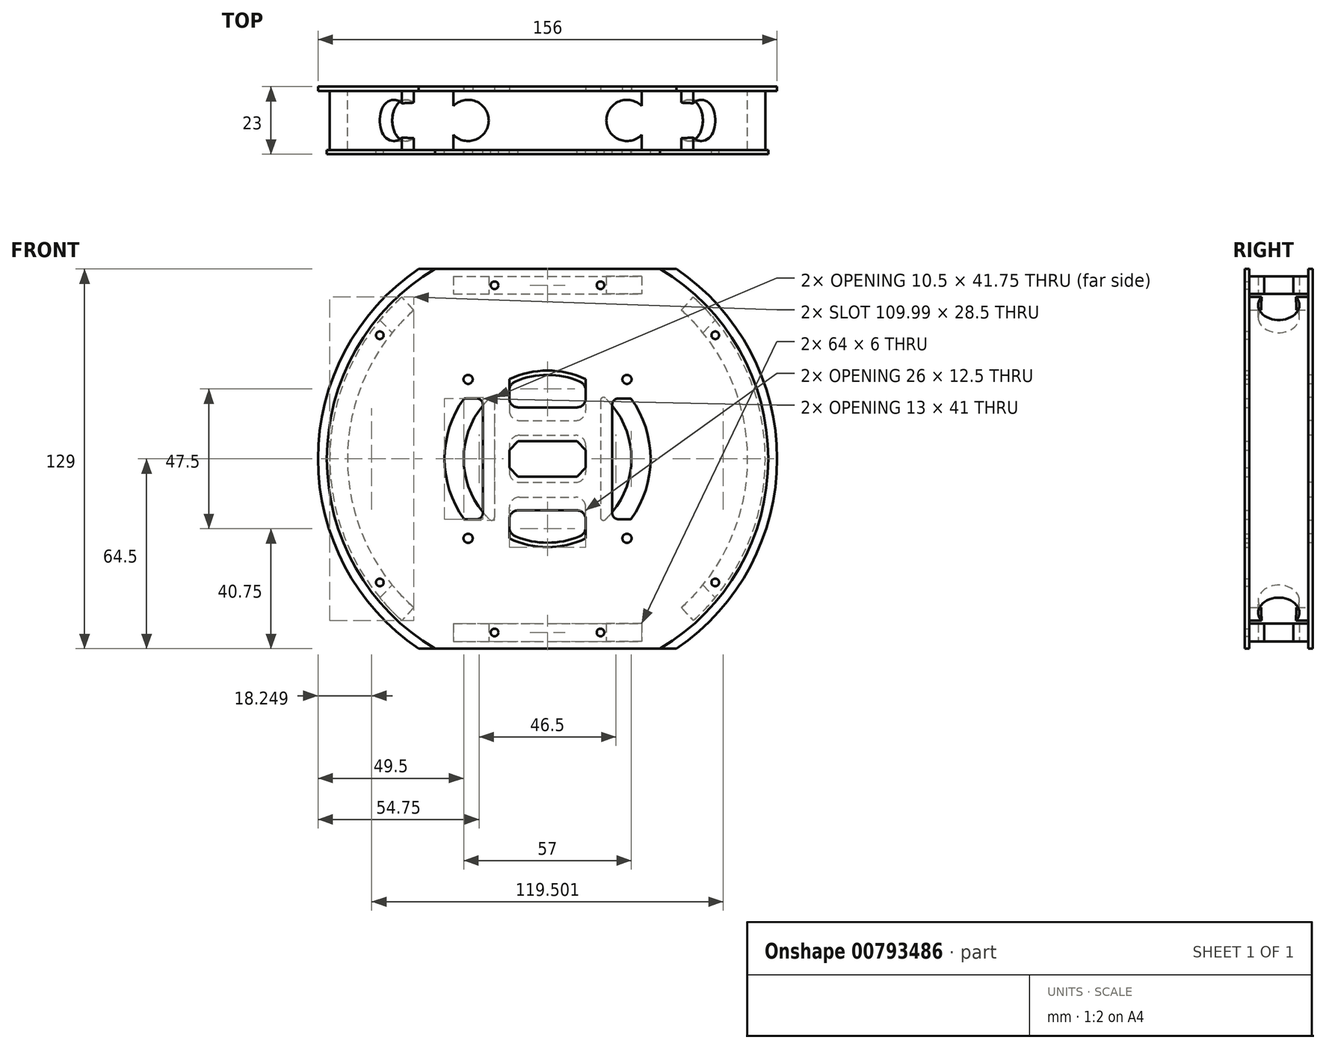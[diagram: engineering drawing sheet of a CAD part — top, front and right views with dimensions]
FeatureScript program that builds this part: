
annotation { "Feature Type Name" : "Feature", "Feature Type Description" : "" }
export const myFeature = defineFeature(function(context is Context, id is Id, definition is map)
    precondition{}
    {
        {
            var Q0;
            Q0=qCreatedBy(makeId("Front.planeOp"),FACE);
            var sketch = newSketch(context, id + "F0", { "sketchPlane" : qUnion([Q0])});
            skLineSegment(sketch, "E0", {"start": v(-78, 0) * mm, "end": v(78, 0) * mm, "construction": true});
            skArc(sketch, "E1", {"start": v(-43.86, 64.5) * mm, "mid": v(-78, 0) * mm, "end": v(-43.86, -64.5) * mm});
            skLineSegment(sketch, "E2", {"start": v(0, 78) * mm, "end": v(0, -78) * mm, "construction": true});
            skLineSegment(sketch, "E3", {"start": v(-43.86, 64.5) * mm, "end": v(43.86, 64.5) * mm});
            skLineSegment(sketch, "E4", {"start": v(-43.86, -64.5) * mm, "end": v(43.86, -64.5) * mm});
            skArc(sketch, "E5.trimOffspring", {"start": v(43.86, -64.5) * mm, "mid": v(78, 0) * mm, "end": v(43.86, 64.5) * mm});
            skLineSegment(sketch, "E6.bottom", {"start": v(-9.5, 8) * mm, "end": v(9.5, 8) * mm});
            skLineSegment(sketch, "E6.top", {"start": v(-9.5, -8) * mm, "end": v(9.5, -8) * mm});
            skLineSegment(sketch, "E6.left", {"start": v(-13, 4.5) * mm, "end": v(-13, -4.5) * mm});
            skLineSegment(sketch, "E6.right", {"start": v(13, 4.5) * mm, "end": v(13, -4.5) * mm});
            skPoint(sketch, "E7.visualSharp", {"position": v(-13, 8) * mm});
            skArc(sketch, "E7.filletArc", {"start": v(-9.5, 8) * mm, "mid": v(-11.97, 6.97) * mm, "end": v(-13, 4.5) * mm});
            skArc(sketch, "E8.MirrorCS", {"start": v(9.5, 8) * mm, "mid": v(11.97, 6.97) * mm, "end": v(13, 4.5) * mm});
            skArc(sketch, "E9.MirrorCS", {"start": v(9.5, -8) * mm, "mid": v(11.97, -6.97) * mm, "end": v(13, -4.5) * mm});
            skArc(sketch, "E10.MirrorCS", {"start": v(-9.5, -8) * mm, "mid": v(-11.97, -6.97) * mm, "end": v(-13, -4.5) * mm});
            skLineSegment(sketch, "E11.top", {"start": v(-9.5, 13) * mm, "end": v(9.5, 13) * mm});
            skLineSegment(sketch, "E11.left", {"start": v(-13, 23.12) * mm, "end": v(-13, 16.5) * mm});
            skLineSegment(sketch, "E11.right", {"start": v(13, 23.12) * mm, "end": v(13, 16.5) * mm});
            skArc(sketch, "E12", {"start": v(-19.7, 20.6) * mm, "mid": v(-28.5, 0) * mm, "end": v(-19.7, -20.6) * mm});
            skPoint(sketch, "E13.visualSharp", {"position": v(-13, 13) * mm});
            skArc(sketch, "E13.filletArc", {"start": v(-13, 16.5) * mm, "mid": v(-11.97, 14.03) * mm, "end": v(-9.5, 13) * mm});
            skArc(sketch, "E14.MirrorCS", {"start": v(13, 16.5) * mm, "mid": v(11.97, 14.03) * mm, "end": v(9.5, 13) * mm});
            skLineSegment(sketch, "E15", {"start": v(18, 19.88) * mm, "end": v(18, -19.88) * mm});
            skLineSegment(sketch, "E16.MirrorCS", {"start": v(-18, 19.88) * mm, "end": v(-18, -19.88) * mm});
            skArc(sketch, "E17.trimOffspring", {"start": v(10.83, 26.36) * mm, "mid": v(0, 28.5) * mm, "end": v(-10.83, 26.36) * mm});
            skPoint(sketch, "E18.visualSharp", {"position": v(13, 25.36) * mm});
            skArc(sketch, "E18.filletArc", {"start": v(13, 23.12) * mm, "mid": v(12.4, 25.07) * mm, "end": v(10.83, 26.36) * mm});
            skArc(sketch, "E19.MirrorCS", {"start": v(-13, 23.12) * mm, "mid": v(-12.4, 25.07) * mm, "end": v(-10.83, 26.36) * mm});
            skArc(sketch, "E20.MirrorCS", {"start": v(13, -23.12) * mm, "mid": v(12.4, -25.07) * mm, "end": v(10.83, -26.36) * mm});
            skArc(sketch, "E21.MirrorCS", {"start": v(-13, -23.12) * mm, "mid": v(-12.4, -25.07) * mm, "end": v(-10.83, -26.36) * mm});
            skArc(sketch, "E22.MirrorCS", {"start": v(-13, -16.5) * mm, "mid": v(-11.97, -14.03) * mm, "end": v(-9.5, -13) * mm});
            skLineSegment(sketch, "E23.MirrorCS", {"start": v(-9.5, -13) * mm, "end": v(9.5, -13) * mm});
            skLineSegment(sketch, "E24.MirrorCS", {"start": v(13, -23.12) * mm, "end": v(13, -16.5) * mm});
            skLineSegment(sketch, "E25.MirrorCS", {"start": v(-13, -23.12) * mm, "end": v(-13, -16.5) * mm});
            skArc(sketch, "E26.MirrorCS", {"start": v(13, -16.5) * mm, "mid": v(11.97, -14.03) * mm, "end": v(9.5, -13) * mm});
            skArc(sketch, "E27.trimOffspring", {"start": v(19.7, -20.6) * mm, "mid": v(28.5, 0) * mm, "end": v(19.7, 20.6) * mm});
            skArc(sketch, "E28.trimOffspring", {"start": v(-10.83, -26.36) * mm, "mid": v(0, -28.5) * mm, "end": v(10.83, -26.36) * mm});
            skPoint(sketch, "E29.visualSharp", {"position": v(18, 22.1) * mm});
            skArc(sketch, "E29.filletArc", {"start": v(19.7, 20.6) * mm, "mid": v(18.6, 20.8) * mm, "end": v(18, 19.88) * mm});
            skArc(sketch, "E30.MirrorCS", {"start": v(19.7, -20.6) * mm, "mid": v(18.6, -20.8) * mm, "end": v(18, -19.88) * mm});
            skArc(sketch, "E31.MirrorCS", {"start": v(-19.7, 20.6) * mm, "mid": v(-18.6, 20.8) * mm, "end": v(-18, 19.88) * mm});
            skArc(sketch, "E32.MirrorCS", {"start": v(-19.7, -20.6) * mm, "mid": v(-18.6, -20.8) * mm, "end": v(-18, -19.88) * mm});
            skCircle(sketch, "E33", {"center": v(-27, 27) * mm, "radius": 1.55 * mm});
            skCircle(sketch, "E34.MirrorC", {"center": v(27, 27) * mm, "radius": 1.55 * mm});
            skCircle(sketch, "E35.MirrorC", {"center": v(27, -27) * mm, "radius": 1.55 * mm});
            skCircle(sketch, "E36.MirrorC", {"center": v(-27, -27) * mm, "radius": 1.55 * mm});
            skSolve(sketch);
        }
        {
            var Q0;
            Q0=makeQuery(id+"F0.imprint","IMPRINT",FACE,{"disambiguationData":[TD([[makeQuery(id+"F0.imprint","IMPRINT",EDGE,{"derivedFrom":sQuery(id+"F0.wireOp",EDGE,"E1")}),1.0]])]});
            extrude(context, id + "F1", {"entities" : qUnion([Q0]), "oppositeDirection" : true, "depth" : 11.5 * mm, "offsetDistance" : 25 * mm, "hasSecondDirection" : true, "secondDirectionOppositeDirection" : true, "secondDirectionDepth" : 10 * mm});
        }
        {
            var Q0;
            Q0=qCreatedBy(makeId("Front.planeOp"),FACE);
            var sketch = newSketch(context, id + "F2", { "sketchPlane" : qUnion([Q0])});
            skPoint(sketch, "E37.center", {"position": v(0, 0) * mm});
            skLineSegment(sketch, "E38", {"start": v(-78, 0) * mm, "end": v(78, 0) * mm, "construction": true});
            skLineSegment(sketch, "E39", {"start": v(0, 78) * mm, "end": v(0, -78) * mm, "construction": true});
            skCircle(sketch, "E40", {"center": v(0, 0) * mm, "radius": 78 * mm, "construction": true});
            skLineSegment(sketch, "E41.bottom", {"start": v(-32, -56) * mm, "end": v(32, -56) * mm});
            skLineSegment(sketch, "E41.top", {"start": v(-32, -62) * mm, "end": v(32, -62) * mm});
            skLineSegment(sketch, "E41.left", {"start": v(-32, -56) * mm, "end": v(-32, -62) * mm});
            skLineSegment(sketch, "E41.right", {"start": v(32, -56) * mm, "end": v(32, -62) * mm});
            skLineSegment(sketch, "E42.MirrorCS", {"start": v(32, 56) * mm, "end": v(32, 62) * mm});
            skLineSegment(sketch, "E43.MirrorCS", {"start": v(-32, 56) * mm, "end": v(-32, 62) * mm});
            skLineSegment(sketch, "E44.MirrorCS", {"start": v(-32, 62) * mm, "end": v(32, 62) * mm});
            skLineSegment(sketch, "E45.MirrorCS", {"start": v(-32, 56) * mm, "end": v(32, 56) * mm});
            skCircle(sketch, "E46", {"center": v(0, 0) * mm, "radius": 75 * mm, "construction": true});
            skArc(sketch, "E47", {"start": v(-49.52, 55) * mm, "mid": v(-74, 0) * mm, "end": v(-49.52, -55) * mm});
            skArc(sketch, "E48", {"start": v(-45.5, 50.53) * mm, "mid": v(-68, 0) * mm, "end": v(-45.5, -50.53) * mm});
            skLineSegment(sketch, "E49", {"start": v(45.5, -50.53) * mm, "end": v(49.52, -55) * mm});
            skLineSegment(sketch, "E50.MirrorCS", {"start": v(45.5, 50.53) * mm, "end": v(49.52, 55) * mm});
            skLineSegment(sketch, "E51.MirrorCS", {"start": v(-45.5, -50.53) * mm, "end": v(-49.52, -55) * mm});
            skLineSegment(sketch, "E52.MirrorCS", {"start": v(-45.5, 50.53) * mm, "end": v(-49.52, 55) * mm});
            skArc(sketch, "E53.trimOffspring", {"start": v(45.5, -50.53) * mm, "mid": v(68, 0) * mm, "end": v(45.5, 50.53) * mm});
            skArc(sketch, "E54.trimOffspring", {"start": v(49.52, -55) * mm, "mid": v(74, 0) * mm, "end": v(49.52, 55) * mm});
            skLineSegment(sketch, "E55", {"start": v(0, 0) * mm, "end": v(47.38, 47.38) * mm, "construction": true});
            skLineSegment(sketch, "E56", {"start": v(52.33, 52.33) * mm, "end": v(47.38, 47.38) * mm});
            skLineSegment(sketch, "E57", {"start": v(47.38, 47.38) * mm, "end": v(42.43, 52.33) * mm});
            skLineSegment(sketch, "E58", {"start": v(42.43, 52.33) * mm, "end": v(47.38, 57.28) * mm});
            skLineSegment(sketch, "E59", {"start": v(47.38, 57.28) * mm, "end": v(52.33, 52.33) * mm});
            skLineSegment(sketch, "E60.MirrorCS", {"start": v(-47.38, 57.28) * mm, "end": v(-52.33, 52.33) * mm});
            skLineSegment(sketch, "E61.MirrorCS", {"start": v(-52.33, 52.33) * mm, "end": v(-47.38, 47.38) * mm});
            skLineSegment(sketch, "E62.MirrorCS", {"start": v(-42.43, 52.33) * mm, "end": v(-47.38, 57.28) * mm});
            skLineSegment(sketch, "E63.MirrorCS", {"start": v(-47.38, 47.38) * mm, "end": v(-42.43, 52.33) * mm});
            skLineSegment(sketch, "E64.MirrorCS", {"start": v(52.33, -52.33) * mm, "end": v(47.38, -47.38) * mm});
            skLineSegment(sketch, "E65.MirrorCS", {"start": v(47.38, -47.38) * mm, "end": v(42.43, -52.33) * mm});
            skLineSegment(sketch, "E66.MirrorCS", {"start": v(42.43, -52.33) * mm, "end": v(47.38, -57.28) * mm});
            skLineSegment(sketch, "E67.MirrorCS", {"start": v(47.38, -57.28) * mm, "end": v(52.33, -52.33) * mm});
            skLineSegment(sketch, "E68.MirrorCS", {"start": v(-52.33, -52.33) * mm, "end": v(-47.38, -47.38) * mm});
            skLineSegment(sketch, "E69.MirrorCS", {"start": v(-47.38, -47.38) * mm, "end": v(-42.43, -52.33) * mm});
            skLineSegment(sketch, "E70.MirrorCS", {"start": v(-42.43, -52.33) * mm, "end": v(-47.38, -57.28) * mm});
            skLineSegment(sketch, "E71.MirrorCS", {"start": v(-47.38, -57.28) * mm, "end": v(-52.33, -52.33) * mm});
            skLineSegment(sketch, "E72", {"start": v(-27, 62) * mm, "end": v(-27, 56) * mm});
            skLineSegment(sketch, "E73.MirrorCS", {"start": v(27, 62) * mm, "end": v(27, 56) * mm});
            skLineSegment(sketch, "E74.MirrorCS", {"start": v(27, -62) * mm, "end": v(27, -56) * mm});
            skLineSegment(sketch, "E75.MirrorCS", {"start": v(-27, -62) * mm, "end": v(-27, -56) * mm});
            skLineSegment(sketch, "E76", {"start": v(-20, 62) * mm, "end": v(-20, 56) * mm});
            skLineSegment(sketch, "E77.MirrorCS", {"start": v(20, 62) * mm, "end": v(20, 56) * mm});
            skLineSegment(sketch, "E78.MirrorCS", {"start": v(-20, -62) * mm, "end": v(-20, -56) * mm});
            skLineSegment(sketch, "E79.MirrorCS", {"start": v(20, -62) * mm, "end": v(20, -56) * mm});
            skSolve(sketch);
        }
        {
            var Q0;
            Q0=makeQuery(id+"F2.imprint","IMPRINT",FACE,{"disambiguationData":[TD([[makeQuery(id+"F2.imprint","IMPRINT",EDGE,{"derivedFrom":sQuery(id+"F2.wireOp",EDGE,"E47")}),1.0]])]});
            var Q1;
            Q1=makeQuery(id+"F2.imprint","IMPRINT",FACE,{"disambiguationData":[TD([[makeQuery(id+"F2.imprint","IMPRINT",EDGE,{"derivedFrom":sQuery(id+"F2.wireOp",EDGE,"E49")}),1.0]])]});
            var Q2;
            Q2=makeQuery(id+"F2.imprint","IMPRINT",FACE,{"disambiguationData":[TD([[makeQuery(id+"F2.imprint","IMPRINT",EDGE,{"derivedFrom":sQuery(id+"F2.wireOp",EDGE,"E41.bottom")}),-1.0]])]});
            var Q3;
            {var subQ0=sQuery(id+"F2.wireOp",EDGE,"E50.MirrorCS");Q3=makeQuery(id+"F2.imprint","IMPRINT",FACE,{"disambiguationData":[TD([[makeQuery(id+"F2.imprint","IMPRINT",EDGE,{"derivedFrom":subQ0}),-1.0]])]});}
            var Q4;
            {var subQ0=sQuery(id+"F2.wireOp",EDGE,"E64.MirrorCS");var subQ1=sQuery(id+"F2.wireOp",EDGE,"E53.trimOffspring");var subQ2=makeQuery(id+"F2.imprint","INTERSECT",VERTEX,{"derivedFrom":[subQ1,subQ0]});Q4=makeQuery(id+"F2.imprint","IMPRINT",FACE,{"disambiguationData":[TD([[makeQuery(id+"F2.imprint","IMPRINT",EDGE,{"disambiguationData":[TD([[subQ2,-1.0]])],"derivedFrom":subQ1}),-1.0]])]});}
            var Q5;
            {var subQ0=sQuery(id+"F2.wireOp",EDGE,"E72");Q5=makeQuery(id+"F2.imprint","IMPRINT",FACE,{"disambiguationData":[TD([[makeQuery(id+"F2.imprint","IMPRINT",EDGE,{"derivedFrom":subQ0}),1.0]])]});}
            var Q6;
            {var subQ0=sQuery(id+"F2.wireOp",EDGE,"E76");Q6=makeQuery(id+"F2.imprint","IMPRINT",FACE,{"disambiguationData":[TD([[makeQuery(id+"F2.imprint","IMPRINT",EDGE,{"derivedFrom":subQ0}),1.0]])]});}
            var Q7;
            {var subQ0=sQuery(id+"F2.wireOp",EDGE,"E73.MirrorCS");Q7=makeQuery(id+"F2.imprint","IMPRINT",FACE,{"disambiguationData":[TD([[makeQuery(id+"F2.imprint","IMPRINT",EDGE,{"derivedFrom":subQ0}),-1.0]])]});}
            var Q8;
            {var subQ0=sQuery(id+"F2.wireOp",EDGE,"E42.MirrorCS");Q8=makeQuery(id+"F2.imprint","IMPRINT",FACE,{"disambiguationData":[TD([[makeQuery(id+"F2.imprint","IMPRINT",EDGE,{"derivedFrom":subQ0}),1.0]])]});}
            var Q9;
            {var subQ0=sQuery(id+"F2.wireOp",EDGE,"E43.MirrorCS");Q9=makeQuery(id+"F2.imprint","IMPRINT",FACE,{"disambiguationData":[TD([[makeQuery(id+"F2.imprint","IMPRINT",EDGE,{"derivedFrom":subQ0}),-1.0]])]});}
            extrude(context, id + "F3", {"entities" : qUnion([Q0, Q1, Q2, Q3, Q4, Q5, Q6, Q7, Q8, Q9]), "operationType" : NewBodyOperationType.ADD, "endBound" : BoundingType.SYMMETRIC, "depth" : 20 * mm, "offsetDistance" : 25 * mm});
        }
        {
            var Q0;
            {var subQ1=sQuery(id+"F2.wireOp",EDGE,"E50.MirrorCS");Q0=makeQuery(id+"F2.imprint","IMPRINT",FACE,{"disambiguationData":[TD([[makeQuery(id+"F2.imprint","IMPRINT",EDGE,{"derivedFrom":subQ1}),1.0]])]});}
            var Q1;
            {var subQ0=sQuery(id+"F2.wireOp",EDGE,"E50.MirrorCS");Q1=makeQuery(id+"F2.imprint","IMPRINT",FACE,{"disambiguationData":[TD([[makeQuery(id+"F2.imprint","IMPRINT",EDGE,{"derivedFrom":subQ0}),-1.0]])]});}
            var Q2;
            {var subQ0=sQuery(id+"F2.wireOp",EDGE,"E51.MirrorCS");Q2=makeQuery(id+"F2.imprint","IMPRINT",FACE,{"disambiguationData":[TD([[makeQuery(id+"F2.imprint","IMPRINT",EDGE,{"derivedFrom":subQ0}),1.0]])]});}
            var Q3;
            {var subQ0=sQuery(id+"F2.wireOp",EDGE,"E51.MirrorCS");Q3=makeQuery(id+"F2.imprint","IMPRINT",FACE,{"disambiguationData":[TD([[makeQuery(id+"F2.imprint","IMPRINT",EDGE,{"derivedFrom":subQ0}),-1.0]])]});}
            var Q4;
            Q4=sQuery(id+"F2.wireOp",EDGE,"E55");
            revolve(context, id + "F4", {"operationType" : NewBodyOperationType.REMOVE, "surfaceOperationType" : NewSurfaceOperationType.NEW, "entities" : qUnion([Q0, Q1, Q2, Q3]), "axis" : qUnion([Q4]), "revolveType" : RevolveType.FULL, "oppositeDirection" : true});
        }
        {
            var Q0;
            {var subQ1=sQuery(id+"F2.wireOp",EDGE,"E52.MirrorCS");Q0=makeQuery(id+"F2.imprint","IMPRINT",FACE,{"disambiguationData":[TD([[makeQuery(id+"F2.imprint","IMPRINT",EDGE,{"derivedFrom":subQ1}),-1.0]])]});}
            var Q1;
            {var subQ0=sQuery(id+"F2.wireOp",EDGE,"E52.MirrorCS");Q1=makeQuery(id+"F2.imprint","IMPRINT",FACE,{"disambiguationData":[TD([[makeQuery(id+"F2.imprint","IMPRINT",EDGE,{"derivedFrom":subQ0}),1.0]])]});}
            var Q2;
            {var subQ5=sQuery(id+"F2.wireOp",EDGE,"E49");Q2=makeQuery(id+"F2.imprint","IMPRINT",FACE,{"disambiguationData":[TD([[makeQuery(id+"F2.imprint","IMPRINT",EDGE,{"derivedFrom":subQ5}),-1.0]])]});}
            var Q3;
            {var subQ0=sQuery(id+"F2.wireOp",EDGE,"E49");Q3=makeQuery(id+"F2.imprint","IMPRINT",FACE,{"disambiguationData":[TD([[makeQuery(id+"F2.imprint","IMPRINT",EDGE,{"derivedFrom":subQ0}),1.0]])]});}
            var Q4;
            Q4=sQuery(id+"F2.wireOp",EDGE,"E64.MirrorCS");
            revolve(context, id + "F5", {"operationType" : NewBodyOperationType.REMOVE, "surfaceOperationType" : NewSurfaceOperationType.NEW, "entities" : qUnion([Q0, Q1, Q2, Q3]), "axis" : qUnion([Q4]), "revolveType" : RevolveType.FULL});
        }
        {
            var Q0;
            {var subQ0=sQuery(id+"F2.wireOp",EDGE,"E72");Q0=makeQuery(id+"F2.imprint","IMPRINT",FACE,{"disambiguationData":[TD([[makeQuery(id+"F2.imprint","IMPRINT",EDGE,{"derivedFrom":subQ0}),1.0]])]});}
            var Q1;
            {var subQ0=sQuery(id+"F2.wireOp",EDGE,"E75.MirrorCS");Q1=makeQuery(id+"F2.imprint","IMPRINT",FACE,{"disambiguationData":[TD([[makeQuery(id+"F2.imprint","IMPRINT",EDGE,{"derivedFrom":subQ0}),-1.0]])]});}
            var Q2;
            Q2=sQuery(id+"F2.wireOp",EDGE,"E72");
            revolve(context, id + "F6", {"operationType" : NewBodyOperationType.REMOVE, "surfaceOperationType" : NewSurfaceOperationType.NEW, "entities" : qUnion([Q0, Q1]), "axis" : qUnion([Q2]), "revolveType" : RevolveType.FULL, "oppositeDirection" : true});
        }
        {
            var Q0;
            {var subQ0=sQuery(id+"F2.wireOp",EDGE,"E73.MirrorCS");Q0=makeQuery(id+"F2.imprint","IMPRINT",FACE,{"disambiguationData":[TD([[makeQuery(id+"F2.imprint","IMPRINT",EDGE,{"derivedFrom":subQ0}),-1.0]])]});}
            var Q1;
            {var subQ0=sQuery(id+"F2.wireOp",EDGE,"E74.MirrorCS");Q1=makeQuery(id+"F2.imprint","IMPRINT",FACE,{"disambiguationData":[TD([[makeQuery(id+"F2.imprint","IMPRINT",EDGE,{"derivedFrom":subQ0}),1.0]])]});}
            var Q2;
            Q2=sQuery(id+"F2.wireOp",EDGE,"E73.MirrorCS");
            revolve(context, id + "F7", {"operationType" : NewBodyOperationType.REMOVE, "surfaceOperationType" : NewSurfaceOperationType.NEW, "entities" : qUnion([Q0, Q1]), "axis" : qUnion([Q2]), "revolveType" : RevolveType.FULL, "oppositeDirection" : true});
        }
        {
            var Q0;
            Q0=makeQuery(id+"F3.opExtrude","CAP_FACE",FACE,{"disambiguationData":[OSD([sQuery(id+"F2.wireOp",EDGE,"E42.MirrorCS"),sQuery(id+"F2.wireOp",EDGE,"E43.MirrorCS"),sQuery(id+"F2.wireOp",EDGE,"E44.MirrorCS"),sQuery(id+"F2.wireOp",EDGE,"E45.MirrorCS")])],"isStart":false});
            var sketch = newSketch(context, id + "F8", { "sketchPlane" : qUnion([Q0])});
            skArc(sketch, "E80", {"start": v(-38.27, 64.5) * mm, "mid": v(-75, 0) * mm, "end": v(-38.27, -64.5) * mm});
            skLineSegment(sketch, "E81", {"start": v(-38.27, 64.5) * mm, "end": v(38.27, 64.5) * mm});
            skLineSegment(sketch, "E82", {"start": v(-38.27, -64.5) * mm, "end": v(38.27, -64.5) * mm});
            skArc(sketch, "E83.trimOffspring", {"start": v(38.27, -64.5) * mm, "mid": v(75, 0) * mm, "end": v(38.27, 64.5) * mm});
            skLineSegment(sketch, "E84.bottom", {"start": v(-10, 6) * mm, "end": v(10, 6) * mm});
            skLineSegment(sketch, "E84.top", {"start": v(-10, -6) * mm, "end": v(10, -6) * mm});
            skLineSegment(sketch, "E84.left", {"start": v(-13, 3) * mm, "end": v(-13, -3) * mm});
            skLineSegment(sketch, "E84.right", {"start": v(13, 3) * mm, "end": v(13, -3) * mm});
            skLineSegment(sketch, "E85", {"start": v(-75, 0) * mm, "end": v(75, 0) * mm, "construction": true});
            skLineSegment(sketch, "E86", {"start": v(0, 64.5) * mm, "end": v(0, -64.5) * mm, "construction": true});
            skLineSegment(sketch, "E87", {"start": v(10, 6) * mm, "end": v(13, 3) * mm});
            skLineSegment(sketch, "E88.MirrorCS", {"start": v(-10, 6) * mm, "end": v(-13, 3) * mm});
            skLineSegment(sketch, "E89.MirrorCS", {"start": v(10, -6) * mm, "end": v(13, -3) * mm});
            skLineSegment(sketch, "E90.MirrorCS", {"start": v(-10, -6) * mm, "end": v(-13, -3) * mm});
            skLineSegment(sketch, "E91", {"start": v(-10, 17.5) * mm, "end": v(10, 17.5) * mm});
            skLineSegment(sketch, "E92", {"start": v(-13, 20.5) * mm, "end": v(-13, 27.04) * mm});
            skLineSegment(sketch, "E93", {"start": v(13, 20.5) * mm, "end": v(13, 27.04) * mm});
            skArc(sketch, "E94", {"start": v(-28.37, 20.5) * mm, "mid": v(-35, 0) * mm, "end": v(-28.37, -20.5) * mm});
            skLineSegment(sketch, "E95", {"start": v(24, -20.5) * mm, "end": v(28.37, -20.5) * mm});
            skLineSegment(sketch, "E96", {"start": v(22, -18.5) * mm, "end": v(22, 18.5) * mm});
            skLineSegment(sketch, "E97", {"start": v(24, 20.5) * mm, "end": v(28.37, 20.5) * mm});
            skArc(sketch, "E98.trimOffspring", {"start": v(28.37, -20.5) * mm, "mid": v(35, 0) * mm, "end": v(28.37, 20.5) * mm});
            skArc(sketch, "E99", {"start": v(-13, -27.04) * mm, "mid": v(0, -30) * mm, "end": v(13, -27.04) * mm});
            skArc(sketch, "E100.trimOffspring", {"start": v(13, 27.04) * mm, "mid": v(0, 30) * mm, "end": v(-13, 27.04) * mm});
            skCircle(sketch, "E101", {"center": v(-27, 27) * mm, "radius": 1.55 * mm});
            skCircle(sketch, "E102.MirrorC", {"center": v(27, 27) * mm, "radius": 1.55 * mm});
            skCircle(sketch, "E103.MirrorC", {"center": v(27, -27) * mm, "radius": 1.55 * mm});
            skCircle(sketch, "E104.MirrorC", {"center": v(-27, -27) * mm, "radius": 1.55 * mm});
            skCircle(sketch, "E105", {"center": v(-57, 42) * mm, "radius": 1.3 * mm});
            skCircle(sketch, "E106.MirrorC", {"center": v(57, 42) * mm, "radius": 1.3 * mm});
            skCircle(sketch, "E107.MirrorC", {"center": v(57, -42) * mm, "radius": 1.3 * mm});
            skCircle(sketch, "E108.MirrorC", {"center": v(-57, -42) * mm, "radius": 1.3 * mm});
            skCircle(sketch, "E109", {"center": v(-18, 59) * mm, "radius": 1.3 * mm});
            skCircle(sketch, "E110.MirrorC", {"center": v(18, 59) * mm, "radius": 1.3 * mm});
            skCircle(sketch, "E111.MirrorC", {"center": v(18, -59) * mm, "radius": 1.3 * mm});
            skCircle(sketch, "E112.MirrorC", {"center": v(-18, -59) * mm, "radius": 1.3 * mm});
            skPoint(sketch, "E113.visualSharp", {"position": v(-13, 17.5) * mm});
            skArc(sketch, "E113.filletArc", {"start": v(-13, 20.5) * mm, "mid": v(-12.12, 18.38) * mm, "end": v(-10, 17.5) * mm});
            skArc(sketch, "E114.MirrorCS", {"start": v(13, 20.5) * mm, "mid": v(12.12, 18.38) * mm, "end": v(10, 17.5) * mm});
            skLineSegment(sketch, "E115.MirrorCS", {"start": v(13, -20.5) * mm, "end": v(13, -27.04) * mm});
            skArc(sketch, "E116.MirrorCS", {"start": v(13, -20.5) * mm, "mid": v(12.12, -18.38) * mm, "end": v(10, -17.5) * mm});
            skLineSegment(sketch, "E117.MirrorCS", {"start": v(-13, -20.5) * mm, "end": v(-13, -27.04) * mm});
            skLineSegment(sketch, "E118.MirrorCS", {"start": v(-10, -17.5) * mm, "end": v(10, -17.5) * mm});
            skArc(sketch, "E119.MirrorCS", {"start": v(-13, -20.5) * mm, "mid": v(-12.12, -18.38) * mm, "end": v(-10, -17.5) * mm});
            skPoint(sketch, "E120.visualSharp", {"position": v(22, 20.5) * mm});
            skArc(sketch, "E120.filletArc", {"start": v(24, 20.5) * mm, "mid": v(22.59, 19.91) * mm, "end": v(22, 18.5) * mm});
            skArc(sketch, "E121.MirrorCS", {"start": v(24, -20.5) * mm, "mid": v(22.59, -19.91) * mm, "end": v(22, -18.5) * mm});
            skLineSegment(sketch, "E122.MirrorCS", {"start": v(-24, -20.5) * mm, "end": v(-28.37, -20.5) * mm});
            skArc(sketch, "E123.MirrorCS", {"start": v(-24, -20.5) * mm, "mid": v(-22.59, -19.91) * mm, "end": v(-22, -18.5) * mm});
            skLineSegment(sketch, "E124.MirrorCS", {"start": v(-24, 20.5) * mm, "end": v(-28.37, 20.5) * mm});
            skLineSegment(sketch, "E125.MirrorCS", {"start": v(-22, -18.5) * mm, "end": v(-22, 18.5) * mm});
            skArc(sketch, "E126.MirrorCS", {"start": v(-24, 20.5) * mm, "mid": v(-22.59, 19.91) * mm, "end": v(-22, 18.5) * mm});
            skSolve(sketch);
        }
        {
            var Q0;
            Q0=makeQuery(id+"F8.imprint","IMPRINT",FACE,{"disambiguationData":[TD([[makeQuery(id+"F8.imprint","IMPRINT",EDGE,{"derivedFrom":sQuery(id+"F8.wireOp",EDGE,"E80")}),1.0]])]});
            var Q1;
            Q1=makeQuery(id+"F8.imprint","IMPRINT",FACE,{"disambiguationData":[TD([[makeQuery(id+"F8.imprint","IMPRINT",EDGE,{"derivedFrom":sQuery(id+"F8.wireOp",EDGE,"E109")}),-1.0]])]});
            extrude(context, id + "F9", {"entities" : qUnion([Q0, Q1]), "operationType" : NewBodyOperationType.ADD, "depth" : 1.5 * mm, "offsetDistance" : 25 * mm});
        }
    });
